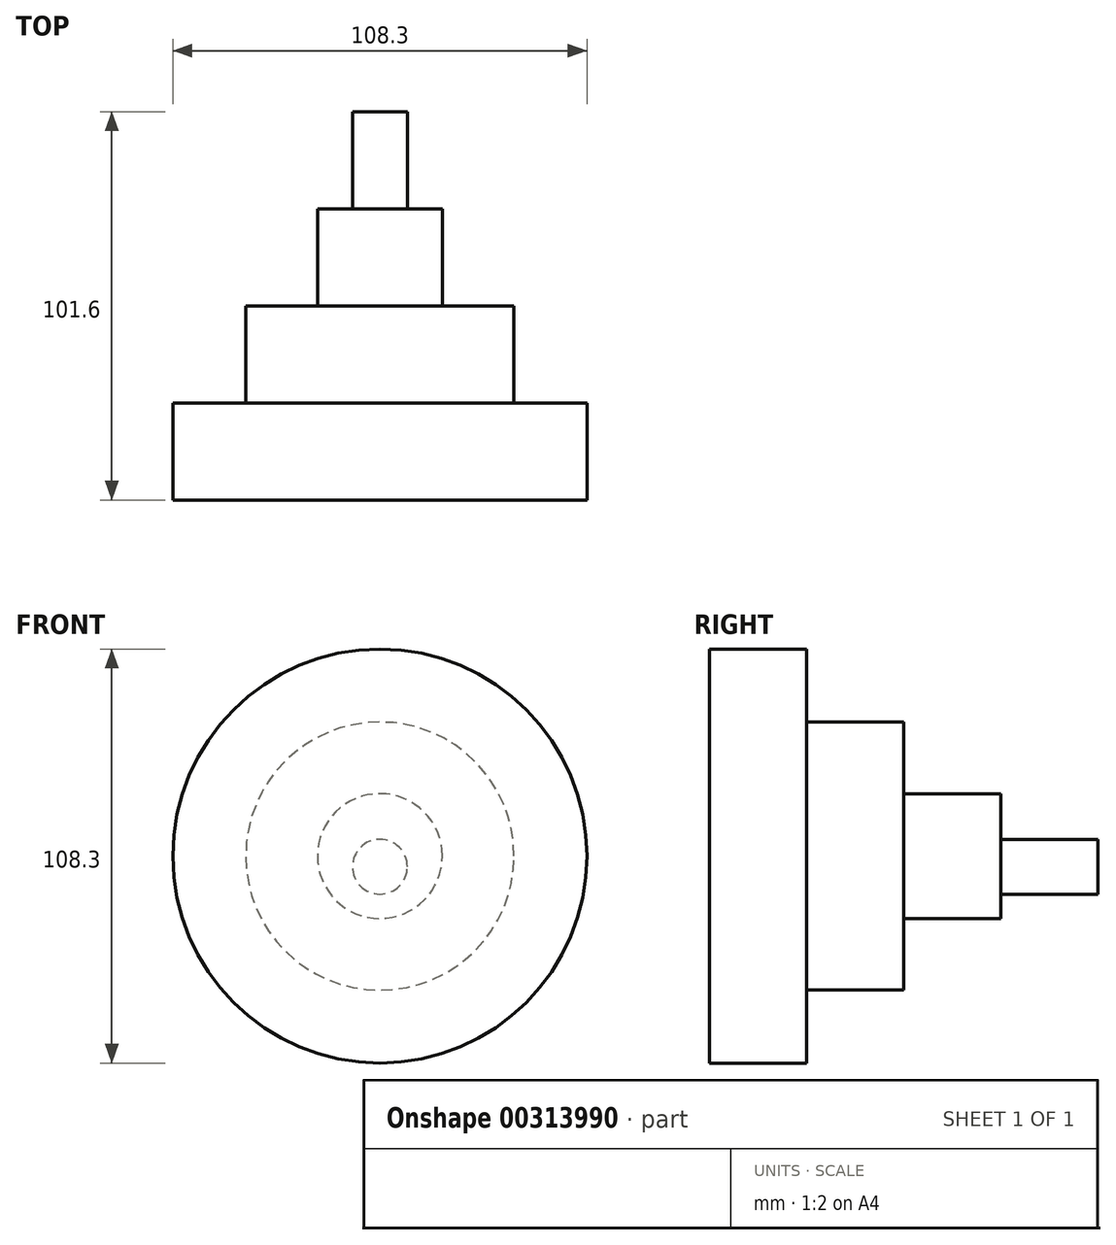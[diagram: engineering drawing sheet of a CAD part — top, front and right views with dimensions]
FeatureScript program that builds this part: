
annotation { "Feature Type Name" : "Feature", "Feature Type Description" : "" }
export const myFeature = defineFeature(function(context is Context, id is Id, definition is map)
    precondition{}
    {
        {
            var Q0;
            Q0=qCreatedBy(makeId("Front.planeOp"),FACE);
            var sketch = newSketch(context, id + "F0", { "sketchPlane" : qUnion([Q0])});
            skCircle(sketch, "E0", {"center": v(0, 0) * mm, "radius": 54.15 * mm});
            skSolve(sketch);
        }
        {
            var Q0;
            Q0 = qSketchRegion(id + "F0", true);
            extrude(context, id + "F1", {"entities" : qUnion([Q0]), "depth" : 25.4 * mm});
        }
        {
            var Q0;
            Q0=makeQuery(id+"F1.opExtrude","CAP_FACE",FACE,{"disambiguationData":[OSD([sQuery(id+"F0.wireOp",EDGE,"E0")])],"isStart":true});
            var sketch = newSketch(context, id + "F2", { "sketchPlane" : qUnion([Q0])});
            skCircle(sketch, "E1.0", {"center": v(0, 0) * mm, "radius": 54.15 * mm});
            skCircle(sketch, "E2", {"center": v(0, 0) * mm, "radius": 35.08 * mm});
            skSolve(sketch);
        }
        {
            var Q0;
            Q0=makeQuery(id+"F2.imprint","IMPRINT",FACE,{"disambiguationData":[TD([[makeQuery(id+"F2.imprint","IMPRINT",EDGE,{"derivedFrom":sQuery(id+"F2.wireOp",EDGE,"E2")}),1.0]])]});
            extrude(context, id + "F3", {"entities" : qUnion([Q0]), "operationType" : NewBodyOperationType.ADD, "depth" : 25.4 * mm});
        }
        {
            var Q0;
            Q0=makeQuery(id+"F3.opExtrude","CAP_FACE",FACE,{"disambiguationData":[OSD([sQuery(id+"F2.wireOp",EDGE,"E2")])],"isStart":false});
            var sketch = newSketch(context, id + "F4", { "sketchPlane" : qUnion([Q0])});
            skCircle(sketch, "E3.0", {"center": v(0, 0) * mm, "radius": 35.08 * mm});
            skCircle(sketch, "E4", {"center": v(0, 0) * mm, "radius": 16.33 * mm});
            skSolve(sketch);
        }
        {
            var Q0;
            Q0=makeQuery(id+"F4.imprint","IMPRINT",FACE,{"disambiguationData":[TD([[makeQuery(id+"F4.imprint","IMPRINT",EDGE,{"derivedFrom":sQuery(id+"F4.wireOp",EDGE,"E4")}),1.0]])]});
            extrude(context, id + "F5", {"entities" : qUnion([Q0]), "operationType" : NewBodyOperationType.ADD, "depth" : 25.4 * mm});
        }
        {
            var Q0;
            Q0=makeQuery(id+"F5.opExtrude","CAP_FACE",FACE,{"disambiguationData":[OSD([sQuery(id+"F4.wireOp",EDGE,"E4")])],"isStart":false});
            var sketch = newSketch(context, id + "F6", { "sketchPlane" : qUnion([Q0])});
            skCircle(sketch, "E5", {"center": v(0, -2.77) * mm, "radius": 7.17 * mm});
            skSolve(sketch);
        }
        {
            var Q0;
            Q0 = qSketchRegion(id + "F6", true);
            extrude(context, id + "F7", {"entities" : qUnion([Q0]), "operationType" : NewBodyOperationType.ADD, "depth" : 25.4 * mm});
        }
    });
